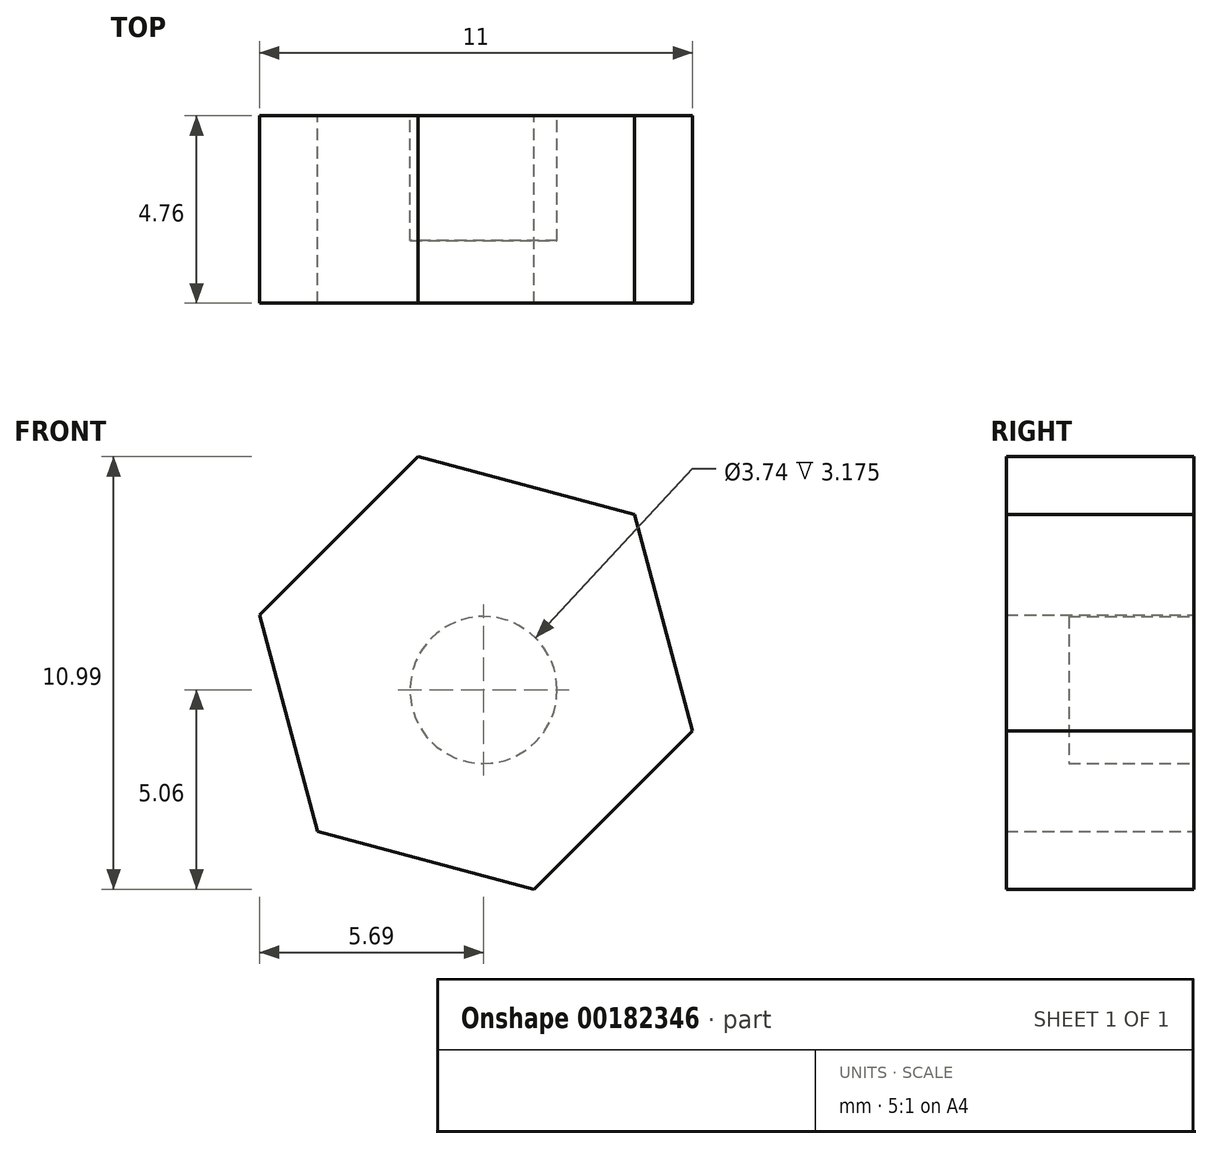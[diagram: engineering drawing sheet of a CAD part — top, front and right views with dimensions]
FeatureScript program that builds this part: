
annotation { "Feature Type Name" : "Feature", "Feature Type Description" : "" }
export const myFeature = defineFeature(function(context is Context, id is Id, definition is map)
    precondition{}
    {
        {
            var Q0;
            Q0=qCreatedBy(makeId("Front.planeOp"),FACE);
            var sketch = newSketch(context, id + "F0", { "sketchPlane" : qUnion([Q0])});
            skCircle(sketch, "E0.cCircle", {"center": v(44.63, 27.91) * mm, "radius": 4.93 * mm, "construction": true});
            skLineSegment(sketch, "E0.0", {"start": v(39.13, 29.39) * mm, "end": v(43.15, 33.41) * mm});
            skLineSegment(sketch, "E0.1", {"start": v(43.15, 33.41) * mm, "end": v(48.65, 31.94) * mm});
            skLineSegment(sketch, "E0.2", {"start": v(48.65, 31.94) * mm, "end": v(50.13, 26.44) * mm});
            skLineSegment(sketch, "E0.3", {"start": v(50.13, 26.44) * mm, "end": v(46.1, 22.42) * mm});
            skLineSegment(sketch, "E0.4", {"start": v(46.1, 22.42) * mm, "end": v(40.6, 23.89) * mm});
            skLineSegment(sketch, "E0.5", {"start": v(40.6, 23.89) * mm, "end": v(39.13, 29.39) * mm});
            skPoint(sketch, "E0.0.midPoint", {"position": v(41.14, 31.4) * mm});
            skSolve(sketch);
        }
        {
            var Q0;
            Q0=makeQuery(id+"F0.imprint","IMPRINT",FACE,{"disambiguationData":[TD([[makeQuery(id+"F0.imprint","IMPRINT",EDGE,{"derivedFrom":sQuery(id+"F0.wireOp",EDGE,"E0.0")}),-1.0]])]});
            extrude(context, id + "F1", {"entities" : qUnion([Q0]), "depth" : 4.76 * mm});
        }
        {
            var Q0;
            Q0=makeQuery(id+"F1.opExtrude","CAP_FACE",FACE,{"disambiguationData":[OSD([sQuery(id+"F0.wireOp",EDGE,"E0.0"),sQuery(id+"F0.wireOp",EDGE,"E0.1"),sQuery(id+"F0.wireOp",EDGE,"E0.2"),sQuery(id+"F0.wireOp",EDGE,"E0.3"),sQuery(id+"F0.wireOp",EDGE,"E0.4"),sQuery(id+"F0.wireOp",EDGE,"E0.5")])],"isStart":true});
            var sketch = newSketch(context, id + "F2", { "sketchPlane" : qUnion([Q0])});
            skCircle(sketch, "E1", {"center": v(-44.82, 27.48) * mm, "radius": 1.87 * mm});
            skSolve(sketch);
        }
        {
            var Q0;
            Q0=makeQuery(id+"F2.imprint","IMPRINT",FACE,{"disambiguationData":[TD([[makeQuery(id+"F2.imprint","IMPRINT",EDGE,{"derivedFrom":sQuery(id+"F2.wireOp",EDGE,"E1")}),1.0]])]});
            extrude(context, id + "F3", {"entities" : qUnion([Q0]), "operationType" : NewBodyOperationType.REMOVE, "oppositeDirection" : true, "depth" : 3.17 * mm});
        }
    });
